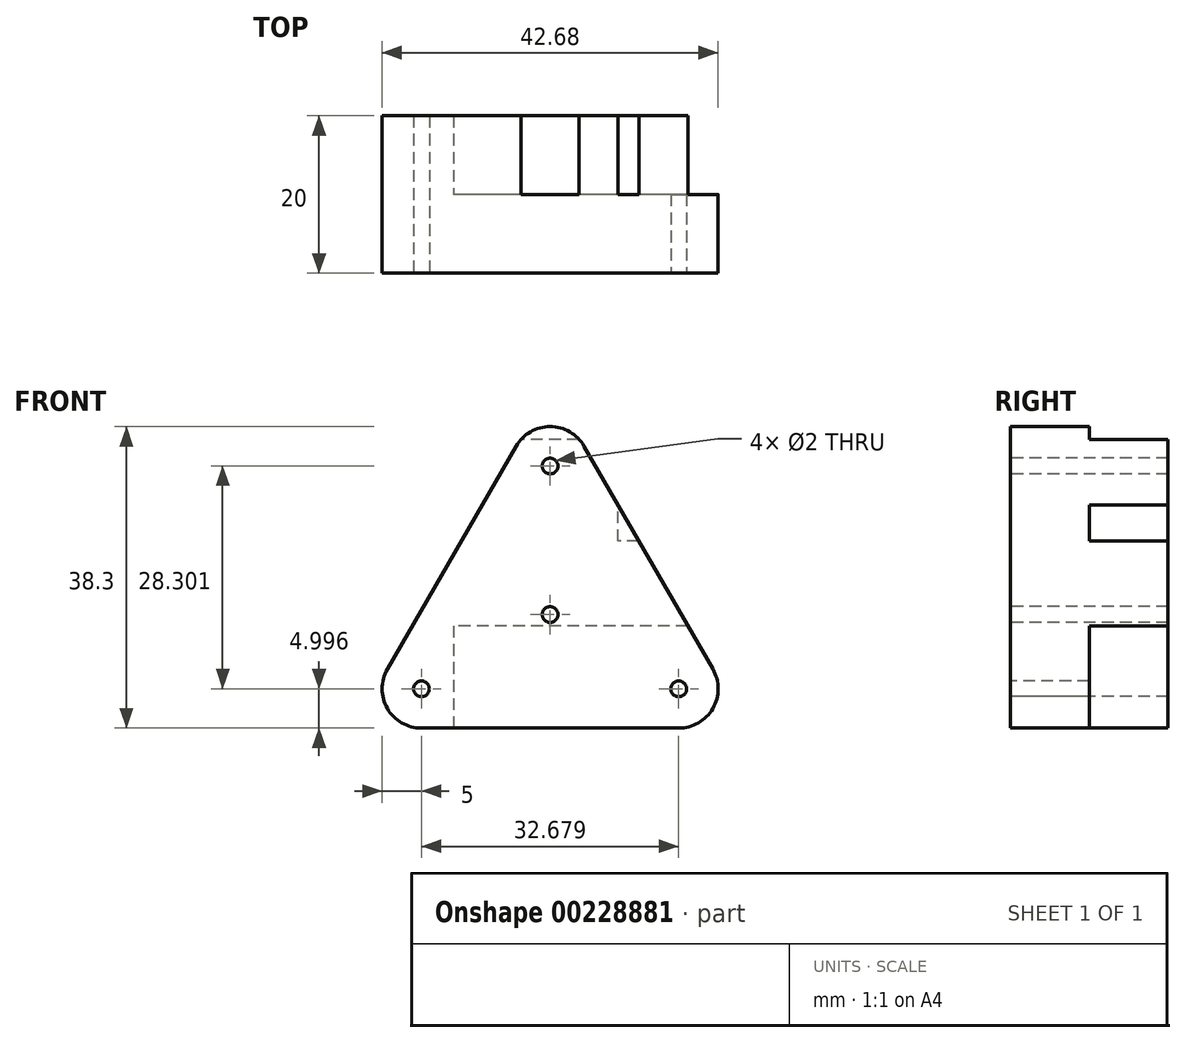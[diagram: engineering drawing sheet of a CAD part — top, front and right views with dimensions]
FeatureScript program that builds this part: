
annotation { "Feature Type Name" : "Feature", "Feature Type Description" : "" }
export const myFeature = defineFeature(function(context is Context, id is Id, definition is map)
    precondition{}
    {
        {
            var Q0;
            Q0=qCreatedBy(makeId("Front.planeOp"),FACE);
            var sketch = newSketch(context, id + "F0", { "sketchPlane" : qUnion([Q0])});
            skCircle(sketch, "E0", {"center": v(0, 0) * mm, "radius": 28.87 * mm, "construction": true});
            skLineSegment(sketch, "E1", {"start": v(-25, -14.43) * mm, "end": v(25, -14.43) * mm, "construction": true});
            skLineSegment(sketch, "E2", {"start": v(25, -14.43) * mm, "end": v(0, 28.87) * mm, "construction": true});
            skLineSegment(sketch, "E3", {"start": v(0, 28.87) * mm, "end": v(-25, -14.43) * mm, "construction": true});
            skCircle(sketch, "E4", {"center": v(-16.34, -9.43) * mm, "radius": 5 * mm, "construction": true});
            skCircle(sketch, "E5", {"center": v(0, 18.87) * mm, "radius": 5 * mm, "construction": true});
            skCircle(sketch, "E6", {"center": v(16.34, -9.43) * mm, "radius": 5 * mm, "construction": true});
            skLineSegment(sketch, "E7", {"start": v(-20.67, -6.93) * mm, "end": v(-4.33, 21.37) * mm});
            skLineSegment(sketch, "E8", {"start": v(4.33, 21.37) * mm, "end": v(20.67, -6.93) * mm});
            skLineSegment(sketch, "E9", {"start": v(16.34, -14.43) * mm, "end": v(-16.34, -14.43) * mm});
            skArc(sketch, "E10", {"start": v(-4.33, 21.37) * mm, "mid": v(0, 23.87) * mm, "end": v(4.33, 21.37) * mm});
            skArc(sketch, "E11", {"start": v(20.67, -6.93) * mm, "mid": v(20.67, -11.93) * mm, "end": v(16.34, -14.43) * mm});
            skArc(sketch, "E12", {"start": v(-16.34, -14.43) * mm, "mid": v(-20.67, -11.93) * mm, "end": v(-20.67, -6.93) * mm});
            skSolve(sketch);
        }
        {
            var Q0;
            Q0=makeQuery(id+"F0.imprint","IMPRINT",FACE,{"disambiguationData":[TD([[makeQuery(id+"F0.imprint","IMPRINT",EDGE,{"derivedFrom":sQuery(id+"F0.wireOp",EDGE,"E7")}),-1.0]])]});
            extrude(context, id + "F1", {"entities" : qUnion([Q0]), "depth" : 10 * mm});
        }
        {
            var Q0;
            Q0=makeQuery(id+"F1.opExtrude","CAP_FACE",FACE,{"disambiguationData":[OSD([sQuery(id+"F0.wireOp",EDGE,"E7"),sQuery(id+"F0.wireOp",EDGE,"E8"),sQuery(id+"F0.wireOp",EDGE,"E9"),sQuery(id+"F0.wireOp",EDGE,"E10"),sQuery(id+"F0.wireOp",EDGE,"E11"),sQuery(id+"F0.wireOp",EDGE,"E12")])],"isStart":false});
            var sketch = newSketch(context, id + "F2", { "sketchPlane" : qUnion([Q0])});
            skPoint(sketch, "E13", {"position": v(0, 18.87) * mm});
            skPoint(sketch, "E14", {"position": v(16.34, -9.43) * mm});
            skPoint(sketch, "E15", {"position": v(-16.34, -9.43) * mm});
            skPoint(sketch, "E16", {"position": v(0, 0) * mm});
            skSolve(sketch);
        }
        {
            var Q0;
            Q0=sQuery(id+"F2.wireOp",VERTEX,"E13");
            var Q1;
            Q1=sQuery(id+"F2.wireOp",VERTEX,"E16");
            var Q2;
            Q2=sQuery(id+"F2.wireOp",VERTEX,"E14");
            var Q3;
            Q3=sQuery(id+"F2.wireOp",VERTEX,"E15");
            var Q4;
            Q4=makeQuery(id+"F1.opExtrude","SWEPT_BODY",BODY,{"disambiguationData":[OSD([sQuery(id+"F0.wireOp",EDGE,"E7"),sQuery(id+"F0.wireOp",EDGE,"E8"),sQuery(id+"F0.wireOp",EDGE,"E9"),sQuery(id+"F0.wireOp",EDGE,"E10"),sQuery(id+"F0.wireOp",EDGE,"E11"),sQuery(id+"F0.wireOp",EDGE,"E12")])]});
            hole(context, id + "F3", {"style" : HoleStyle.SIMPLE, "endStyle" : HoleEndStyle.BLIND, "holeDiameter" : 2 * mm, "holeDepth" : 12 * mm, "locations" : qUnion([Q0, Q1, Q2, Q3]), "scope" : qUnion([Q4])});
        }
        {
            var Q0;
            Q0=makeQuery(id+"F1.opExtrude","CAP_FACE",FACE,{"disambiguationData":[OSD([sQuery(id+"F0.wireOp",EDGE,"E7"),sQuery(id+"F0.wireOp",EDGE,"E8"),sQuery(id+"F0.wireOp",EDGE,"E9"),sQuery(id+"F0.wireOp",EDGE,"E10"),sQuery(id+"F0.wireOp",EDGE,"E11"),sQuery(id+"F0.wireOp",EDGE,"E12")])],"isStart":true});
            var sketch = newSketch(context, id + "F4", { "sketchPlane" : qUnion([Q0])});
            skLineSegment(sketch, "E17", {"start": v(-17.5, -1.43) * mm, "end": v(12.25, -1.43) * mm});
            skLineSegment(sketch, "E18", {"start": v(-11.29, 9.32) * mm, "end": v(-8.65, 9.32) * mm});
            skLineSegment(sketch, "E19", {"start": v(-8.65, 9.32) * mm, "end": v(-8.65, 13.89) * mm});
            skLineSegment(sketch, "E20", {"start": v(-3.67, 22.27) * mm, "end": v(3.67, 22.27) * mm});
            skPoint(sketch, "E21", {"position": v(-18.95, -14.43) * mm});
            skPoint(sketch, "E21.positionSnap0", {"position": v(0, -14.43) * mm});
            skPoint(sketch, "E22", {"position": v(18.95, -14.43) * mm});
            skLineSegment(sketch, "E23", {"start": v(18.95, -14.43) * mm, "end": v(0, -14.43) * mm, "construction": true});
            skLineSegment(sketch, "E24", {"start": v(-18.95, -14.43) * mm, "end": v(0, -14.43) * mm, "construction": true});
            skLineSegment(sketch, "E25", {"start": v(12.25, -1.43) * mm, "end": v(12.25, -14.43) * mm});
            skLineSegment(sketch, "E26", {"start": v(12.25, -14.43) * mm, "end": v(16.34, -14.43) * mm});
            skLineSegment(sketch, "E27", {"start": v(20.67, -6.93) * mm, "end": v(4.33, 21.37) * mm});
            skArc(sketch, "E28", {"start": v(4.33, 21.37) * mm, "mid": v(4.02, 21.84) * mm, "end": v(3.67, 22.27) * mm});
            skArc(sketch, "E29", {"start": v(-4.33, 21.37) * mm, "mid": v(-4.02, 21.84) * mm, "end": v(-3.67, 22.27) * mm});
            skLineSegment(sketch, "E30", {"start": v(-17.5, -1.43) * mm, "end": v(-4.33, 21.37) * mm});
            skArc(sketch, "E31", {"start": v(16.34, -14.43) * mm, "mid": v(20.67, -11.93) * mm, "end": v(20.67, -6.93) * mm});
            skSolve(sketch);
        }
        {
            var Q0;
            Q0=makeQuery(id+"F4.imprint","IMPRINT",FACE,{"disambiguationData":[TD([[makeQuery(id+"F4.imprint","IMPRINT",EDGE,{"derivedFrom":makeQuery(id+"F3.hole-0.boolean.opBoolean","INTERSECT",EDGE,{"derivedFrom":[makeQuery(id+"F1.opExtrude","CAP_FACE",FACE,{"disambiguationData":[OSD([sQuery(id+"F0.wireOp",EDGE,"E7"),sQuery(id+"F0.wireOp",EDGE,"E8"),sQuery(id+"F0.wireOp",EDGE,"E9"),sQuery(id+"F0.wireOp",EDGE,"E10"),sQuery(id+"F0.wireOp",EDGE,"E11"),sQuery(id+"F0.wireOp",EDGE,"E12")])],"isStart":true}),makeQuery(id+"F3.hole-0.opRevolve","SWEPT_FACE",FACE,{"disambiguationData":[OSD([sQuery(id+"F3.hole-0.sketch.wireOp",EDGE,"core_line_2")])]})]})}),1.0]])]});
            var Q1;
            Q1=makeQuery(id+"F4.imprint","IMPRINT",FACE,{"disambiguationData":[TD([[makeQuery(id+"F4.imprint","IMPRINT",EDGE,{"derivedFrom":makeQuery(id+"F3.hole-1.boolean.opBoolean","INTERSECT",EDGE,{"derivedFrom":[makeQuery(id+"F1.opExtrude","CAP_FACE",FACE,{"disambiguationData":[OSD([sQuery(id+"F0.wireOp",EDGE,"E7"),sQuery(id+"F0.wireOp",EDGE,"E8"),sQuery(id+"F0.wireOp",EDGE,"E9"),sQuery(id+"F0.wireOp",EDGE,"E10"),sQuery(id+"F0.wireOp",EDGE,"E11"),sQuery(id+"F0.wireOp",EDGE,"E12")])],"isStart":true}),makeQuery(id+"F3.hole-1.opRevolve","SWEPT_FACE",FACE,{"disambiguationData":[OSD([sQuery(id+"F3.hole-1.sketch.wireOp",EDGE,"core_line_2")])]})]})}),1.0]])]});
            var Q2;
            Q2=makeQuery(id+"F4.imprint","IMPRINT",FACE,{"disambiguationData":[TD([[makeQuery(id+"F4.imprint","IMPRINT",EDGE,{"derivedFrom":makeQuery(id+"F3.hole-3.boolean.opBoolean","INTERSECT",EDGE,{"derivedFrom":[makeQuery(id+"F1.opExtrude","CAP_FACE",FACE,{"disambiguationData":[OSD([sQuery(id+"F0.wireOp",EDGE,"E7"),sQuery(id+"F0.wireOp",EDGE,"E8"),sQuery(id+"F0.wireOp",EDGE,"E9"),sQuery(id+"F0.wireOp",EDGE,"E10"),sQuery(id+"F0.wireOp",EDGE,"E11"),sQuery(id+"F0.wireOp",EDGE,"E12")])],"isStart":true}),makeQuery(id+"F3.hole-3.opRevolve","SWEPT_FACE",FACE,{"disambiguationData":[OSD([sQuery(id+"F3.hole-3.sketch.wireOp",EDGE,"core_line_2")])]})]})}),1.0]])]});
            var Q3;
            {var subQ3=sQuery(id+"F4.wireOp",EDGE,"E17");Q3=makeQuery(id+"F4.imprint","IMPRINT",FACE,{"disambiguationData":[TD([[makeQuery(id+"F4.imprint","IMPRINT",EDGE,{"derivedFrom":subQ3}),1.0]])]});}
            extrude(context, id + "F5", {"entities" : qUnion([Q0, Q1, Q2, Q3]), "operationType" : NewBodyOperationType.ADD, "depth" : 10 * mm});
        }
    });
